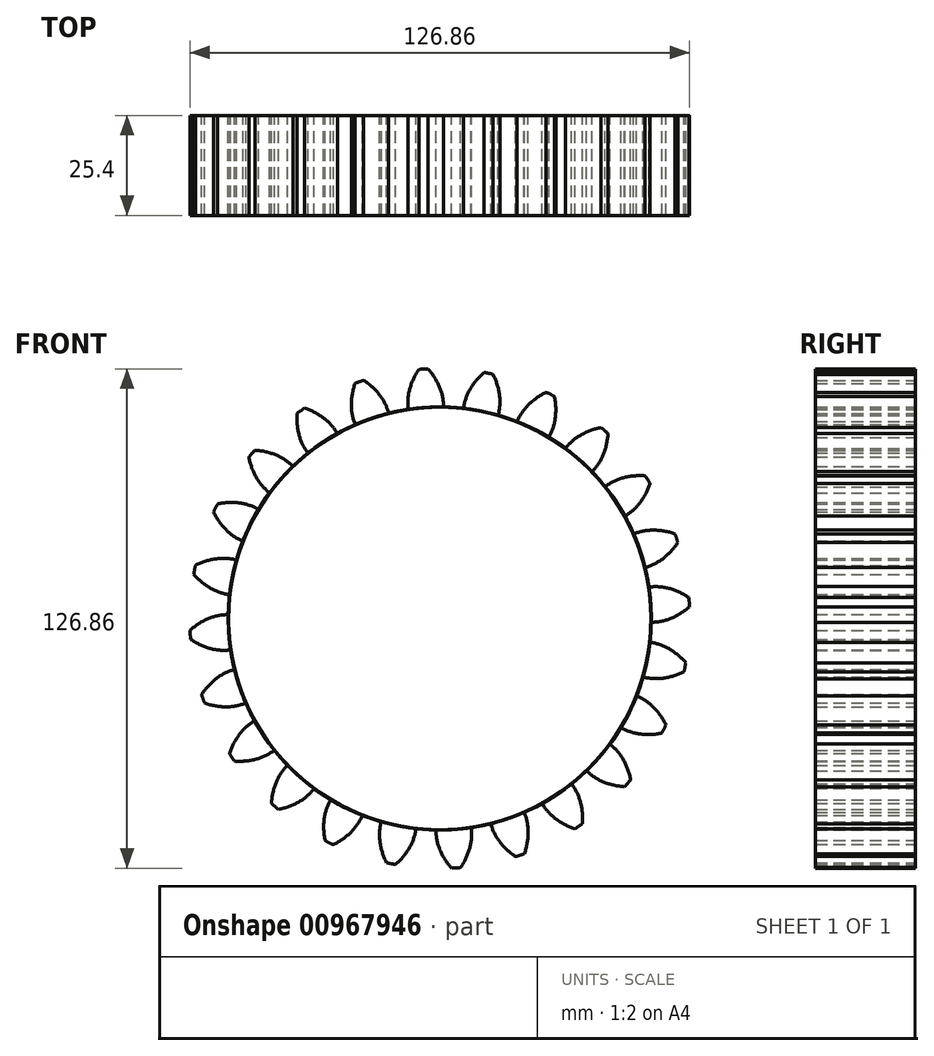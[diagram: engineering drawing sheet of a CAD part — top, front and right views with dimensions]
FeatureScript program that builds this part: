
annotation { "Feature Type Name" : "Feature", "Feature Type Description" : "" }
export const myFeature = defineFeature(function(context is Context, id is Id, definition is map)
    precondition{}
    {
        {
            var Q0;
            Q0=qCreatedBy(makeId("Front.planeOp"),FACE);
            var sketch = newSketch(context, id + "F0", { "sketchPlane" : qUnion([Q0])});
            skCircle(sketch, "E0", {"center": v(0, 0) * mm, "radius": 53.72 * mm});
            skCircle(sketch, "E1", {"center": v(0, 0) * mm, "radius": 58.67 * mm, "construction": true});
            skCircle(sketch, "E2", {"center": v(0, 0) * mm, "radius": 63.5 * mm, "construction": true});
            skLineSegment(sketch, "E3", {"start": v(0, 94.68) * mm, "end": v(0, 0) * mm, "construction": true});
            skLineSegment(sketch, "E4", {"start": v(0, 0) * mm, "end": v(-6.12, 93.45) * mm, "construction": true});
            skLineSegment(sketch, "E5", {"start": v(0, 58.67) * mm, "end": v(-79.6, 58.67) * mm, "construction": true});
            skLineSegment(sketch, "E6", {"start": v(0, 58.67) * mm, "end": v(-77.65, 30.41) * mm, "construction": true});
            skCircle(sketch, "E7", {"center": v(0, 0) * mm, "radius": 55.14 * mm, "construction": true});
            skCircle(sketch, "E8", {"center": v(0, 58.67) * mm, "radius": 14.6 * mm, "construction": true});
            skCircle(sketch, "E9", {"center": v(-13.63, 53.42) * mm, "radius": 14.6 * mm, "construction": true});
            skArc(sketch, "E10", {"start": v(0, 58.67) * mm, "mid": v(-1.3, 61.18) * mm, "end": v(-2.99, 63.43) * mm});
            skArc(sketch, "E11", {"start": v(0.97, 53.71) * mm, "mid": v(0.73, 56.24) * mm, "end": v(0, 58.67) * mm});
            skArc(sketch, "E12.MirrorCS", {"start": v(-7.66, 58.17) * mm, "mid": v(-6.7, 60.82) * mm, "end": v(-5.32, 63.28) * mm});
            skArc(sketch, "E13.MirrorCS", {"start": v(-7.98, 53.13) * mm, "mid": v(-8.07, 55.66) * mm, "end": v(-7.66, 58.17) * mm});
            skArc(sketch, "E14", {"start": v(-2.99, 63.43) * mm, "mid": v(-4.15, 63.38) * mm, "end": v(-5.32, 63.28) * mm});
            skSolve(sketch);
        }
        {
            var Q0;
            Q0=makeQuery(id+"F0.imprint","IMPRINT",FACE,{"disambiguationData":[TD([[makeQuery(id+"F0.imprint","IMPRINT",EDGE,{"derivedFrom":sQuery(id+"F0.wireOp",EDGE,"E10")}),1.0]])]});
            var Q1;
            {var subQ0=sQuery(id+"F0.wireOp",EDGE,"E0");var subQ1=makeQuery(id+"F0.imprint","INTERSECT",VERTEX,{"derivedFrom":[subQ0,sQuery(id+"F0.wireOp",EDGE,"E11")]});Q1=makeQuery(id+"F0.imprint","IMPRINT",FACE,{"disambiguationData":[TD([[makeQuery(id+"F0.imprint","IMPRINT",EDGE,{"disambiguationData":[TD([[subQ1,-1.0]])],"derivedFrom":subQ0}),1.0]])]});}
            extrude(context, id + "F1", {"entities" : qUnion([Q0, Q1]), "depth" : 25.4 * mm, "offsetDistance" : 25.4 * mm});
        }
        {
            var Q0;
            Q0=makeQuery(id+"F1.opExtrude","SWEPT_BODY",BODY,{"disambiguationData":[OSD([sQuery(id+"F0.wireOp",EDGE,"E0"),sQuery(id+"F0.wireOp",EDGE,"E10"),sQuery(id+"F0.wireOp",EDGE,"E11"),sQuery(id+"F0.wireOp",EDGE,"E12.MirrorCS"),sQuery(id+"F0.wireOp",EDGE,"E13.MirrorCS"),sQuery(id+"F0.wireOp",EDGE,"E14")])]});
            var Q1;
            Q1=makeQuery(id+"F1.opExtrude","SWEPT_FACE",FACE,{"disambiguationData":[OSD([sQuery(id+"F0.wireOp",EDGE,"E10")])]});
            var Q2;
            Q2=makeQuery(id+"F1.opExtrude","SWEPT_FACE",FACE,{"disambiguationData":[OSD([sQuery(id+"F0.wireOp",EDGE,"E11")])]});
            var Q3;
            Q3=makeQuery(id+"F1.opExtrude","SWEPT_FACE",FACE,{"disambiguationData":[OSD([sQuery(id+"F0.wireOp",EDGE,"E14")])]});
            var Q4;
            Q4=makeQuery(id+"F1.opExtrude","SWEPT_FACE",FACE,{"disambiguationData":[OSD([sQuery(id+"F0.wireOp",EDGE,"E12.MirrorCS")])]});
            var Q5;
            Q5=makeQuery(id+"F1.opExtrude","SWEPT_FACE",FACE,{"disambiguationData":[OSD([sQuery(id+"F0.wireOp",EDGE,"E13.MirrorCS")])]});
            var Q6;
            Q6=makeQuery(id+"F1.opExtrude","CAP_EDGE",EDGE,{"disambiguationData":[OSD([sQuery(id+"F0.wireOp",EDGE,"E0")])],"isStart":false});
            circularPattern(context, id + "F2", {"entities" : qUnion([Q0]), "axis" : qUnion([Q6]), "angle" : 15 * degree, "instanceCount" : 24, "oppositeDirection" : true});
        }
    });
